# Revit family: CYLINDER 2.25
name_source: partatom
category: Lighting Fixtures
revit_build: Autodesk Revit 2017 (Build: 20181011_1645(x64)
units: mm (PartAtom-declared; Revit-internal decimal feet)

## family parameters
Cut with Voids When Loaded = No
Host = Face
Light Source = Yes
Part Type = Normal
Room Calculation Point = No
Round Connector Dimension = Use Diameter
Shared = Yes

## types (1)
- Natural Brass
    Canopy Width = 0' - 5"
    Color Filter = 16777215
    Cost = 159 $
    Default Elevation = 4' - 0"
    Description = This refined ceiling fixture offers a streamlined take on the classic surface mount. Whether spotlighting areas of interest in public spaces, complimenting a hallway or illuminating a room, its unassuming design makes it suitable for traditional and contemporary spaces alike.

Handcrafted and Manufactured in our Portland, Ore. factory to exacting specifications. A Schoolhouse Electric Original.
    Dimming Lamp Color Temperature Shift = <None>
    Emit Shape Visible in Rendering = No
    Emit from Circle Diameter = 2' - 0"
    Fitter Size = 0' - 2 1/4"
    Height = 0' - 3 1/2"
    Length = 0' - 3 1/2"
    Light Source Symbol Size = 2' - 0"
    Manufacturer = Schoolhouse
    Max Wattage = 100 W
    Model = Cylinder 2.25
    Primary Finishes = Schoolhouse Natural Brass 181-166-66
    Product Material = Brass
    URL = https://www.schoolhouse.com
    Voltage = 120/220V
    Width = 0' - 5"

## geometry (parser evidence)
native form markers: Sweep x4
no freeform markers — native parametric forms only
